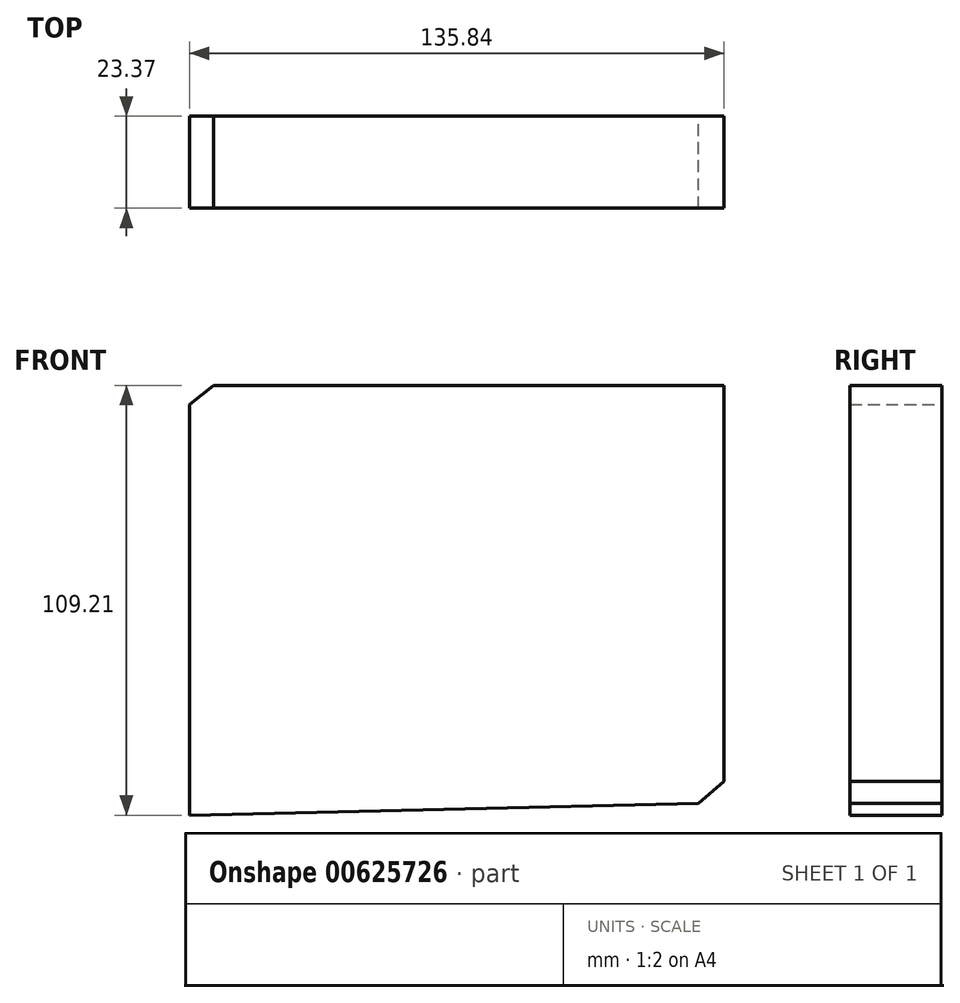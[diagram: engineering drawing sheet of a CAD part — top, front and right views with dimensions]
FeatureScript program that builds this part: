
annotation { "Feature Type Name" : "Feature", "Feature Type Description" : "" }
export const myFeature = defineFeature(function(context is Context, id is Id, definition is map)
    precondition{}
    {
        {
            var Q0;
            Q0=qCreatedBy(makeId("Front.planeOp"),FACE);
            var sketch = newSketch(context, id + "F0", { "sketchPlane" : qUnion([Q0])});
            skLineSegment(sketch, "E0", {"start": v(106.69, -9.38) * mm, "end": v(-22.6, -9.38) * mm});
            skLineSegment(sketch, "E1", {"start": v(106.69, -9.38) * mm, "end": v(106.69, -110.74) * mm});
            skLineSegment(sketch, "E2", {"start": v(-22.6, -9.38) * mm, "end": v(-22.6, -101.02) * mm});
            skLineSegment(sketch, "E3", {"start": v(-22.6, -101.02) * mm, "end": v(-22.6, -113.78) * mm});
            skLineSegment(sketch, "E4", {"start": v(-22.6, -113.78) * mm, "end": v(106.69, -110.74) * mm});
            skLineSegment(sketch, "E5", {"start": v(-22.6, -9.38) * mm, "end": v(-16.51, -4.57) * mm});
            skLineSegment(sketch, "E6", {"start": v(113.23, -4.57) * mm, "end": v(-16.51, -4.57) * mm});
            skLineSegment(sketch, "E7", {"start": v(113.23, -4.57) * mm, "end": v(106.69, -9.38) * mm});
            skLineSegment(sketch, "E8", {"start": v(113.23, -4.57) * mm, "end": v(113.23, -105.18) * mm});
            skLineSegment(sketch, "E9", {"start": v(113.23, -105.18) * mm, "end": v(106.69, -110.74) * mm});
            skLineSegment(sketch, "E10", {"start": v(-16.51, -4.57) * mm, "end": v(-16.51, -105.18) * mm});
            skLineSegment(sketch, "E11", {"start": v(-16.51, -105.18) * mm, "end": v(-22.6, -113.78) * mm});
            skLineSegment(sketch, "E12", {"start": v(-16.51, -105.18) * mm, "end": v(113.23, -105.18) * mm});
            skSolve(sketch);
        }
        {
            var Q0;
            Q0 = qSketchRegion(id + "F0", true);
            var Q1;
            {var subQ1=sQuery(id+"F0.wireOp",EDGE,"E0");var subQ3=sQuery(id+"F0.wireOp",EDGE,"E10");var subQ4=makeQuery(id+"F0.imprint","INTERSECT",VERTEX,{"derivedFrom":[subQ1,subQ3]});Q1=makeQuery(id+"F0.imprint","IMPRINT",FACE,{"disambiguationData":[TD([[makeQuery(id+"F0.imprint","IMPRINT",EDGE,{"disambiguationData":[TD([[subQ4,1.0]])],"derivedFrom":subQ1}),1.0]])]});}
            extrude(context, id + "F1", {"entities" : qUnion([Q0, Q1]), "depth" : 23.37 * mm, "offsetDistance" : 25.4 * mm});
        }
    });
